# Revit family: Mixer-Bath-Dorf Epic-Wall1
name_source: partatom
category: Plumbing Fixtures
revit_build: Autodesk Revit Architecture 2012 (Build: 20110916_2132(x64)
units: mm (PartAtom-declared; Revit-internal decimal feet)

## types (2) — shared parameters
Assembly Code = D2020300
CW Connection = Yes
CWFU = 2
Default Elevation = 600 mm
Description = Fully featured cartridge, Chrome finish, Water efficient, Longer reach for sink versatility, European hoses
HW Connection = Yes
HWFU = 2
Manufacturer = Dorf
Material_ANZRS = Metal-Chrome-Caroma
URL = http://www.dorf.com.au
Vent Connection = No
Waste Connection = No
zero-valued in all types: Cost

## per-type parameters (varying)
| type | Connector Radius | Large | Model | Spout |
| Epic Wall Bath Mixer 180mm Outlet | 0 mm  [stored 0 ft] | No | 6413.04 | 180 mm  [stored 0.590551 ft] |
| Epic Wall Bath Mixer 240mm Outlet | 10 mm  [stored 0.0328084 ft] | Yes | 6414.04 | 240 mm  [stored 0.787402 ft] |

note: column(s) folded — value = type name in every type: Type Comments

note: [stored X ft] marks values corroborated as IEEE doubles in the binary element streams (Revit-internal decimal feet)

## geometry (parser evidence)
native form markers: Blend x4, Sweep x1
no freeform markers — native parametric forms only
